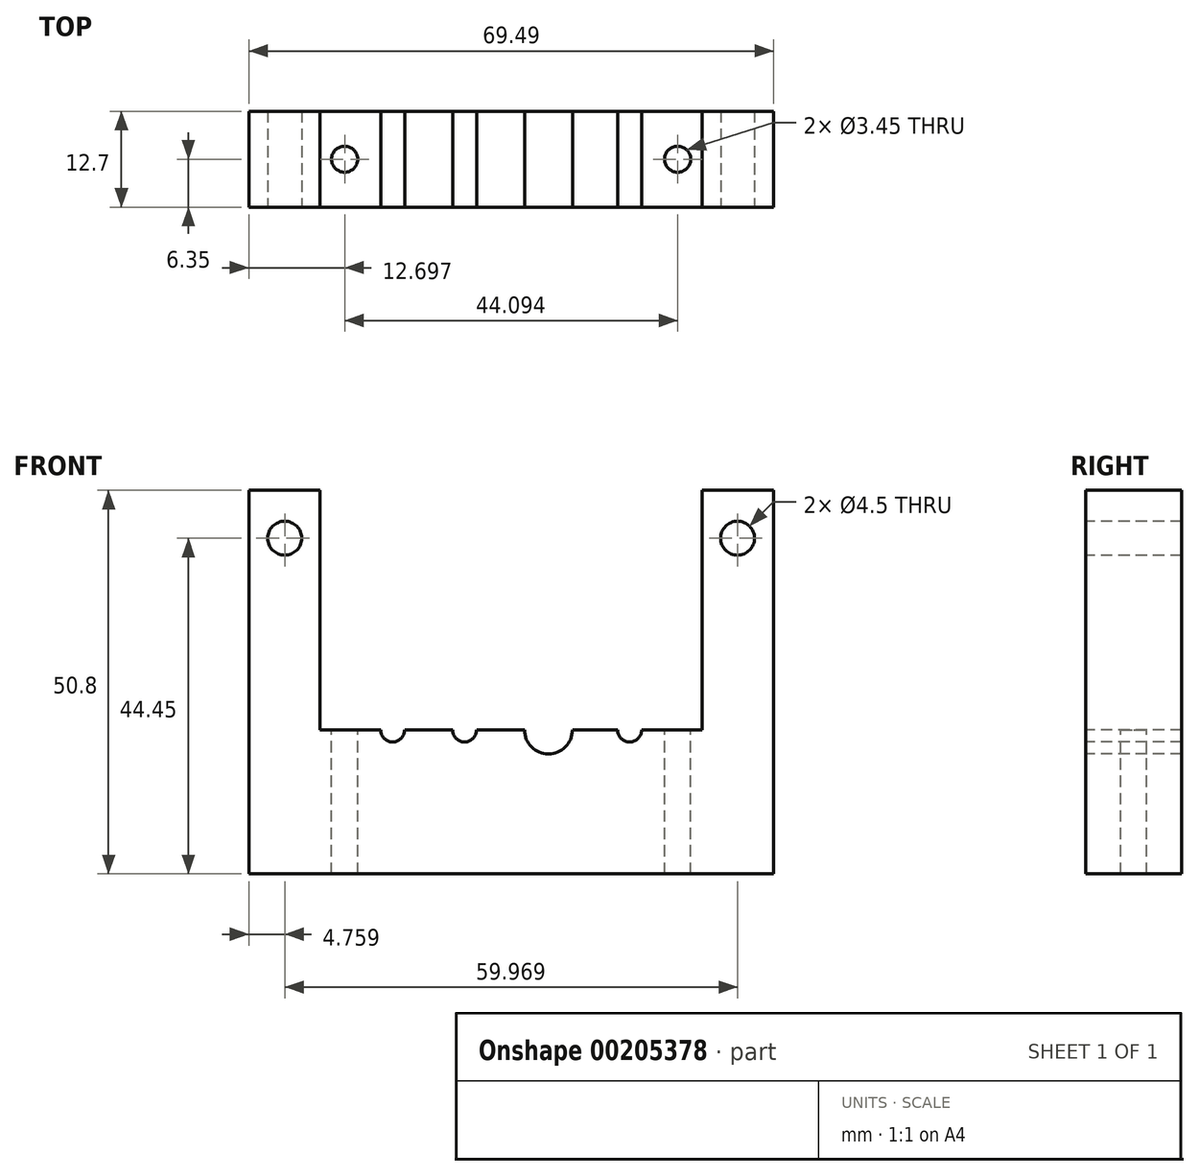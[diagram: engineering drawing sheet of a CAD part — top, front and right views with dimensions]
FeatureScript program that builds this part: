
annotation { "Feature Type Name" : "Feature", "Feature Type Description" : "" }
export const myFeature = defineFeature(function(context is Context, id is Id, definition is map)
    precondition{}
    {
        {
            var Q0;
            Q0=qCreatedBy(makeId("Front.planeOp"),FACE);
            var sketch = newSketch(context, id + "F0", { "sketchPlane" : qUnion([Q0])});
            skLineSegment(sketch, "E0", {"start": v(-47.33, 62.8) * mm, "end": v(-37.88, 62.8) * mm});
            skLineSegment(sketch, "E1", {"start": v(-37.88, 62.8) * mm, "end": v(-37.88, 31.06) * mm});
            skLineSegment(sketch, "E2", {"start": v(-37.88, 31.06) * mm, "end": v(12.71, 31.06) * mm});
            skLineSegment(sketch, "E3", {"start": v(12.71, 31.06) * mm, "end": v(12.71, 62.8) * mm});
            skLineSegment(sketch, "E4", {"start": v(12.71, 62.8) * mm, "end": v(22.16, 62.8) * mm});
            skLineSegment(sketch, "E5", {"start": v(22.16, 62.8) * mm, "end": v(22.16, 12) * mm});
            skLineSegment(sketch, "E6", {"start": v(22.16, 12) * mm, "end": v(-47.33, 12) * mm});
            skLineSegment(sketch, "E7", {"start": v(-47.33, 12) * mm, "end": v(-47.33, 62.8) * mm});
            skSolve(sketch);
        }
        {
            var Q0;
            Q0=makeQuery(id+"F0.imprint","IMPRINT",FACE,{"disambiguationData":[TD([[makeQuery(id+"F0.imprint","IMPRINT",EDGE,{"derivedFrom":sQuery(id+"F0.wireOp",EDGE,"E0")}),-1.0]])]});
            extrude(context, id + "F1", {"entities" : qUnion([Q0]), "depth" : 12.7 * mm});
        }
        {
            var Q0;
            Q0=makeQuery(id+"F1.opExtrude","CAP_FACE",FACE,{"disambiguationData":[OSD([sQuery(id+"F0.wireOp",EDGE,"E0"),sQuery(id+"F0.wireOp",EDGE,"E1"),sQuery(id+"F0.wireOp",EDGE,"E2"),sQuery(id+"F0.wireOp",EDGE,"E3"),sQuery(id+"F0.wireOp",EDGE,"E4"),sQuery(id+"F0.wireOp",EDGE,"E5"),sQuery(id+"F0.wireOp",EDGE,"E6"),sQuery(id+"F0.wireOp",EDGE,"E7")])],"isStart":false});
            var sketch = newSketch(context, id + "F2", { "sketchPlane" : qUnion([Q0])});
            skPoint(sketch, "E8", {"position": v(-28.28, 31.06) * mm});
            skPoint(sketch, "E9", {"position": v(3.1, 31.06) * mm});
            skCircle(sketch, "E10", {"center": v(-28.28, 31.06) * mm, "radius": 1.59 * mm});
            skPoint(sketch, "E11", {"position": v(-18.76, 31.06) * mm});
            skCircle(sketch, "E12", {"center": v(-18.76, 31.06) * mm, "radius": 1.59 * mm});
            skCircle(sketch, "E13", {"center": v(3.1, 31.06) * mm, "radius": 1.59 * mm});
            skCircle(sketch, "E14", {"center": v(-7.65, 31.06) * mm, "radius": 3.18 * mm});
            skSolve(sketch);
        }
        {
            var Q0;
            Q0=sQuery(id+"F2.wireOp",VERTEX,"E8");
            var Q1;
            Q1=sQuery(id+"F2.wireOp",VERTEX,"E11");
            var Q2;
            Q2=sQuery(id+"F2.wireOp",VERTEX,"E9");
            var Q3;
            Q3=makeQuery(id+"F1.opExtrude","SWEPT_BODY",BODY,{"disambiguationData":[OSD([sQuery(id+"F0.wireOp",EDGE,"E0"),sQuery(id+"F0.wireOp",EDGE,"E1"),sQuery(id+"F0.wireOp",EDGE,"E2"),sQuery(id+"F0.wireOp",EDGE,"E3"),sQuery(id+"F0.wireOp",EDGE,"E4"),sQuery(id+"F0.wireOp",EDGE,"E5"),sQuery(id+"F0.wireOp",EDGE,"E6"),sQuery(id+"F0.wireOp",EDGE,"E7")])]});
            hole(context, id + "F3", {"style" : HoleStyle.SIMPLE, "endStyle" : HoleEndStyle.THROUGH, "holeDiameter" : 3.17 * mm, "startFromSketch" : true, "locations" : qUnion([Q0, Q1, Q2]), "scope" : qUnion([Q3]), "isTappedThrough" : true});
        }
        {
            var Q0;
            Q0=sQuery(id+"F2.wireOp",VERTEX,"E14.center");
            var Q1;
            Q1=makeQuery(id+"F1.opExtrude","SWEPT_BODY",BODY,{"disambiguationData":[OSD([sQuery(id+"F0.wireOp",EDGE,"E0"),sQuery(id+"F0.wireOp",EDGE,"E1"),sQuery(id+"F0.wireOp",EDGE,"E2"),sQuery(id+"F0.wireOp",EDGE,"E3"),sQuery(id+"F0.wireOp",EDGE,"E4"),sQuery(id+"F0.wireOp",EDGE,"E5"),sQuery(id+"F0.wireOp",EDGE,"E6"),sQuery(id+"F0.wireOp",EDGE,"E7")])]});
            hole(context, id + "F4", {"style" : HoleStyle.SIMPLE, "endStyle" : HoleEndStyle.THROUGH, "holeDiameter" : 6.35 * mm, "startFromSketch" : true, "locations" : qUnion([Q0]), "scope" : qUnion([Q1]), "isTappedThrough" : true});
        }
        {
            var Q0;
            Q0=makeQuery(id+"F1.opExtrude","CAP_FACE",FACE,{"disambiguationData":[OSD([sQuery(id+"F0.wireOp",EDGE,"E0"),sQuery(id+"F0.wireOp",EDGE,"E1"),sQuery(id+"F0.wireOp",EDGE,"E2"),sQuery(id+"F0.wireOp",EDGE,"E3"),sQuery(id+"F0.wireOp",EDGE,"E4"),sQuery(id+"F0.wireOp",EDGE,"E5"),sQuery(id+"F0.wireOp",EDGE,"E6"),sQuery(id+"F0.wireOp",EDGE,"E7")])],"isStart":false});
            var sketch = newSketch(context, id + "F5", { "sketchPlane" : qUnion([Q0])});
            skPoint(sketch, "E15", {"position": v(-42.57, 56.46) * mm});
            skPoint(sketch, "E16", {"position": v(17.4, 56.46) * mm});
            skSolve(sketch);
        }
        {
            var Q0;
            Q0=sQuery(id+"F5.wireOp",VERTEX,"E15");
            var Q1;
            Q1=sQuery(id+"F5.wireOp",VERTEX,"E16");
            var Q2;
            Q2=makeQuery(id+"F1.opExtrude","SWEPT_BODY",BODY,{"disambiguationData":[OSD([sQuery(id+"F0.wireOp",EDGE,"E0"),sQuery(id+"F0.wireOp",EDGE,"E1"),sQuery(id+"F0.wireOp",EDGE,"E2"),sQuery(id+"F0.wireOp",EDGE,"E3"),sQuery(id+"F0.wireOp",EDGE,"E4"),sQuery(id+"F0.wireOp",EDGE,"E5"),sQuery(id+"F0.wireOp",EDGE,"E6"),sQuery(id+"F0.wireOp",EDGE,"E7")])]});
            hole(context, id + "F6", {"style" : HoleStyle.SIMPLE, "endStyle" : HoleEndStyle.THROUGH, "standardTappedOrClearance" : lookupTablePath({ "standard" : "ANSI", "fit" : "Normal (ASME)", "size" : "#8", "type" : "Clearance" }), "standardBlindInLast" : lookupTablePath({ "fit" : "Free", "standard" : "ANSI", "size" : "#8", "type" : "Clearance" }), "holeDiameter" : 4.5 * mm, "startFromSketch" : true, "locations" : qUnion([Q0, Q1]), "scope" : qUnion([Q2]), "isTappedThrough" : true});
        }
        {
            var Q0;
            {var subQ5=sQuery(id+"F0.wireOp",EDGE,"E2");var subQ6=sQuery(id+"F0.wireOp",EDGE,"E1");Q0=makeQuery(id+"F3.hole-0.boolean.opBoolean","SPLIT",FACE,{"disambiguationData":[TD([makeQuery(id+"F1.opExtrude","SWEPT_FACE",FACE,{"disambiguationData":[OSD([subQ6])]})])],"derivedFrom":makeQuery(id+"F1.opExtrude","SWEPT_FACE",FACE,{"disambiguationData":[OSD([subQ5])]})});}
            var sketch = newSketch(context, id + "F7", { "sketchPlane" : qUnion([Q0])});
            skPoint(sketch, "E17", {"position": v(-34.63, -6.35) * mm});
            skPoint(sketch, "E18", {"position": v(-29.87, -6.35) * mm});
            skSolve(sketch);
        }
        {
            var Q0;
            Q0=sQuery(id+"F7.wireOp",VERTEX,"E17");
            var Q1;
            Q1=makeQuery(id+"F1.opExtrude","SWEPT_BODY",BODY,{"disambiguationData":[OSD([sQuery(id+"F0.wireOp",EDGE,"E0"),sQuery(id+"F0.wireOp",EDGE,"E1"),sQuery(id+"F0.wireOp",EDGE,"E2"),sQuery(id+"F0.wireOp",EDGE,"E3"),sQuery(id+"F0.wireOp",EDGE,"E4"),sQuery(id+"F0.wireOp",EDGE,"E5"),sQuery(id+"F0.wireOp",EDGE,"E6"),sQuery(id+"F0.wireOp",EDGE,"E7")])]});
            hole(context, id + "F8", {"style" : HoleStyle.SIMPLE, "endStyle" : HoleEndStyle.THROUGH, "standardTappedOrClearance" : lookupTablePath({ "standard" : "ANSI", "engagement" : "75%", "pitch" : "32 tpi", "size" : "#8", "type" : "Tapped" }), "standardBlindInLast" : lookupTablePath({ "standard" : "ANSI", "engagement" : "75%", "pitch" : "32 tpi", "size" : "#8", "type" : "Tapped" }), "holeDiameter" : 3.45 * mm, "startFromSketch" : true, "locations" : qUnion([Q0]), "scope" : qUnion([Q1]), "isTappedThrough" : true, "majorDiameter" : 4.17 * mm, "showTappedDepth" : true});
        }
        {
            var Q0;
            {var subQ4=sQuery(id+"F0.wireOp",EDGE,"E3");var subQ5=sQuery(id+"F0.wireOp",EDGE,"E2");var subQ10=makeQuery(id+"F1.opExtrude","SWEPT_FACE",FACE,{"disambiguationData":[OSD([subQ4])]});Q0=makeQuery(id+"F3.hole-2.boolean.opBoolean","SPLIT",FACE,{"disambiguationData":[TD([subQ10])],"derivedFrom":makeQuery(id+"F3.hole-1.boolean.opBoolean","SPLIT",FACE,{"disambiguationData":[TD([subQ10])],"derivedFrom":makeQuery(id+"F3.hole-0.boolean.opBoolean","SPLIT",FACE,{"disambiguationData":[TD([subQ10])],"derivedFrom":makeQuery(id+"F1.opExtrude","SWEPT_FACE",FACE,{"disambiguationData":[OSD([subQ5])]})})})});}
            var sketch = newSketch(context, id + "F9", { "sketchPlane" : qUnion([Q0])});
            skPoint(sketch, "E19", {"position": v(9.46, -6.35) * mm});
            skPoint(sketch, "E20", {"position": v(4.69, -6.35) * mm});
            skSolve(sketch);
        }
        {
            var Q0;
            Q0=sQuery(id+"F9.wireOp",VERTEX,"E19");
            var Q1;
            Q1=makeQuery(id+"F1.opExtrude","SWEPT_BODY",BODY,{"disambiguationData":[OSD([sQuery(id+"F0.wireOp",EDGE,"E0"),sQuery(id+"F0.wireOp",EDGE,"E1"),sQuery(id+"F0.wireOp",EDGE,"E2"),sQuery(id+"F0.wireOp",EDGE,"E3"),sQuery(id+"F0.wireOp",EDGE,"E4"),sQuery(id+"F0.wireOp",EDGE,"E5"),sQuery(id+"F0.wireOp",EDGE,"E6"),sQuery(id+"F0.wireOp",EDGE,"E7")])]});
            hole(context, id + "F10", {"style" : HoleStyle.SIMPLE, "endStyle" : HoleEndStyle.THROUGH, "standardTappedOrClearance" : lookupTablePath({ "standard" : "ANSI", "engagement" : "75%", "pitch" : "32 tpi", "size" : "#8", "type" : "Tapped" }), "standardBlindInLast" : lookupTablePath({ "standard" : "ANSI", "engagement" : "75%", "pitch" : "32 tpi", "size" : "#8", "type" : "Tapped" }), "holeDiameter" : 3.45 * mm, "startFromSketch" : true, "locations" : qUnion([Q0]), "scope" : qUnion([Q1]), "isTappedThrough" : true, "majorDiameter" : 4.17 * mm, "showTappedDepth" : true});
        }
    });
